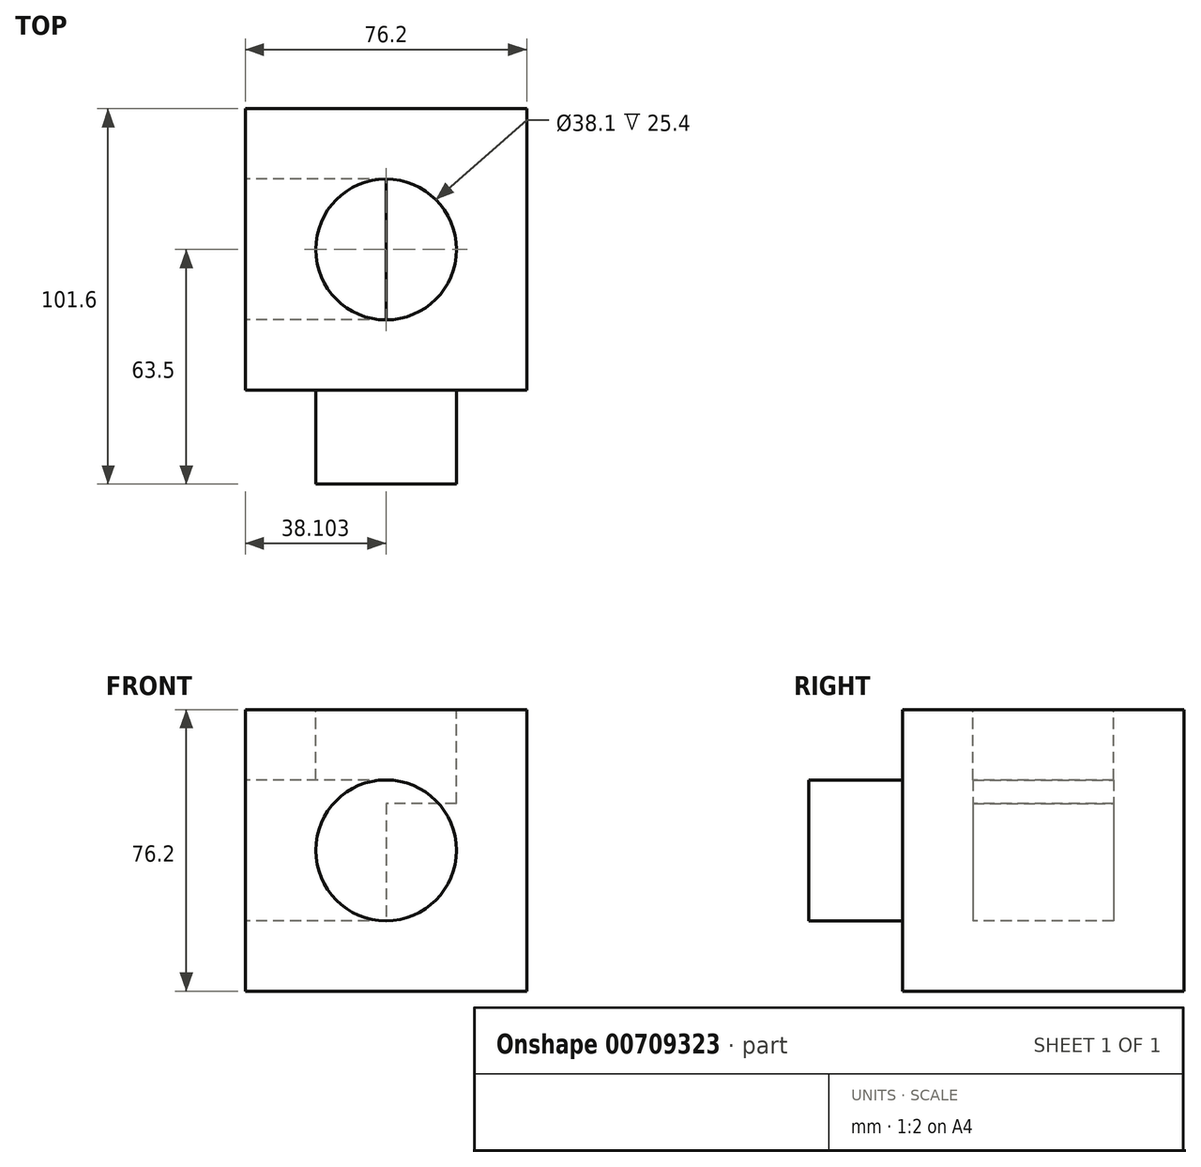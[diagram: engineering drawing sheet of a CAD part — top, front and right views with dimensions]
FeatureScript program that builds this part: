
annotation { "Feature Type Name" : "Feature", "Feature Type Description" : "" }
export const myFeature = defineFeature(function(context is Context, id is Id, definition is map)
    precondition{}
    {
        {
            var Q0;
            Q0=qCreatedBy(makeId("Front.planeOp"),FACE);
            var sketch = newSketch(context, id + "F0", { "sketchPlane" : qUnion([Q0])});
            skLineSegment(sketch, "E0.bottom", {"start": v(-33.72, 42.62) * mm, "end": v(42.48, 42.62) * mm});
            skLineSegment(sketch, "E0.top", {"start": v(-33.72, -33.58) * mm, "end": v(42.48, -33.58) * mm});
            skLineSegment(sketch, "E0.left", {"start": v(-33.72, 42.62) * mm, "end": v(-33.72, -33.58) * mm});
            skLineSegment(sketch, "E0.right", {"start": v(42.48, 42.62) * mm, "end": v(42.48, -33.58) * mm});
            skSolve(sketch);
        }
        {
            var Q0;
            Q0=makeQuery(id+"F0.imprint","IMPRINT",FACE,{"disambiguationData":[TD([[makeQuery(id+"F0.imprint","IMPRINT",EDGE,{"derivedFrom":sQuery(id+"F0.wireOp",EDGE,"E0.bottom")}),-1.0]])]});
            extrude(context, id + "F1", {"entities" : qUnion([Q0]), "depth" : 76.2 * mm, "offsetDistance" : 25.4 * mm});
        }
        {
            var Q0;
            Q0=makeQuery(id+"F1.opExtrude","CAP_FACE",FACE,{"disambiguationData":[OSD([sQuery(id+"F0.wireOp",EDGE,"E0.bottom"),sQuery(id+"F0.wireOp",EDGE,"E0.top"),sQuery(id+"F0.wireOp",EDGE,"E0.left"),sQuery(id+"F0.wireOp",EDGE,"E0.right")])],"isStart":false});
            var sketch = newSketch(context, id + "F2", { "sketchPlane" : qUnion([Q0])});
            skCircle(sketch, "E1", {"center": v(4.38, 4.52) * mm, "radius": 19.05 * mm});
            skSolve(sketch);
        }
        {
            var Q0;
            Q0=makeQuery(id+"F2.imprint","IMPRINT",FACE,{"disambiguationData":[TD([[makeQuery(id+"F2.imprint","IMPRINT",EDGE,{"derivedFrom":sQuery(id+"F2.wireOp",EDGE,"E1")}),1.0]])]});
            extrude(context, id + "F3", {"entities" : qUnion([Q0]), "operationType" : NewBodyOperationType.ADD, "depth" : 25.4 * mm, "offsetDistance" : 25.4 * mm});
        }
        {
            var Q0;
            Q0=makeQuery(id+"F1.opExtrude","SWEPT_FACE",FACE,{"disambiguationData":[OSD([sQuery(id+"F0.wireOp",EDGE,"E0.bottom")])]});
            var sketch = newSketch(context, id + "F4", { "sketchPlane" : qUnion([Q0])});
            skCircle(sketch, "E2", {"center": v(4.38, -38.1) * mm, "radius": 19.05 * mm});
            skSolve(sketch);
        }
        {
            var Q0;
            Q0=makeQuery(id+"F4.imprint","IMPRINT",FACE,{"disambiguationData":[TD([[makeQuery(id+"F4.imprint","IMPRINT",EDGE,{"derivedFrom":sQuery(id+"F4.wireOp",EDGE,"E2")}),1.0]])]});
            extrude(context, id + "F5", {"entities" : qUnion([Q0]), "operationType" : NewBodyOperationType.REMOVE, "oppositeDirection" : true, "depth" : 25.4 * mm, "offsetDistance" : 25.4 * mm});
        }
        {
            var Q0;
            Q0=makeQuery(id+"F1.opExtrude","SWEPT_FACE",FACE,{"disambiguationData":[OSD([sQuery(id+"F0.wireOp",EDGE,"E0.left")])]});
            var sketch = newSketch(context, id + "F6", { "sketchPlane" : qUnion([Q0])});
            skLineSegment(sketch, "E3.bottom", {"start": v(19.05, 23.57) * mm, "end": v(57.15, 23.57) * mm});
            skLineSegment(sketch, "E3.top", {"start": v(19.05, -14.53) * mm, "end": v(57.15, -14.53) * mm});
            skLineSegment(sketch, "E3.left", {"start": v(19.05, 23.57) * mm, "end": v(19.05, -14.53) * mm});
            skLineSegment(sketch, "E3.right", {"start": v(57.15, 23.57) * mm, "end": v(57.15, -14.53) * mm});
            skSolve(sketch);
        }
        {
            var Q0;
            Q0=makeQuery(id+"F6.imprint","IMPRINT",FACE,{"disambiguationData":[TD([[makeQuery(id+"F6.imprint","IMPRINT",EDGE,{"derivedFrom":sQuery(id+"F6.wireOp",EDGE,"E3.bottom")}),-1.0]])]});
            extrude(context, id + "F7", {"entities" : qUnion([Q0]), "operationType" : NewBodyOperationType.REMOVE, "oppositeDirection" : true, "depth" : 38.1 * mm, "offsetDistance" : 25.4 * mm});
        }
    });
